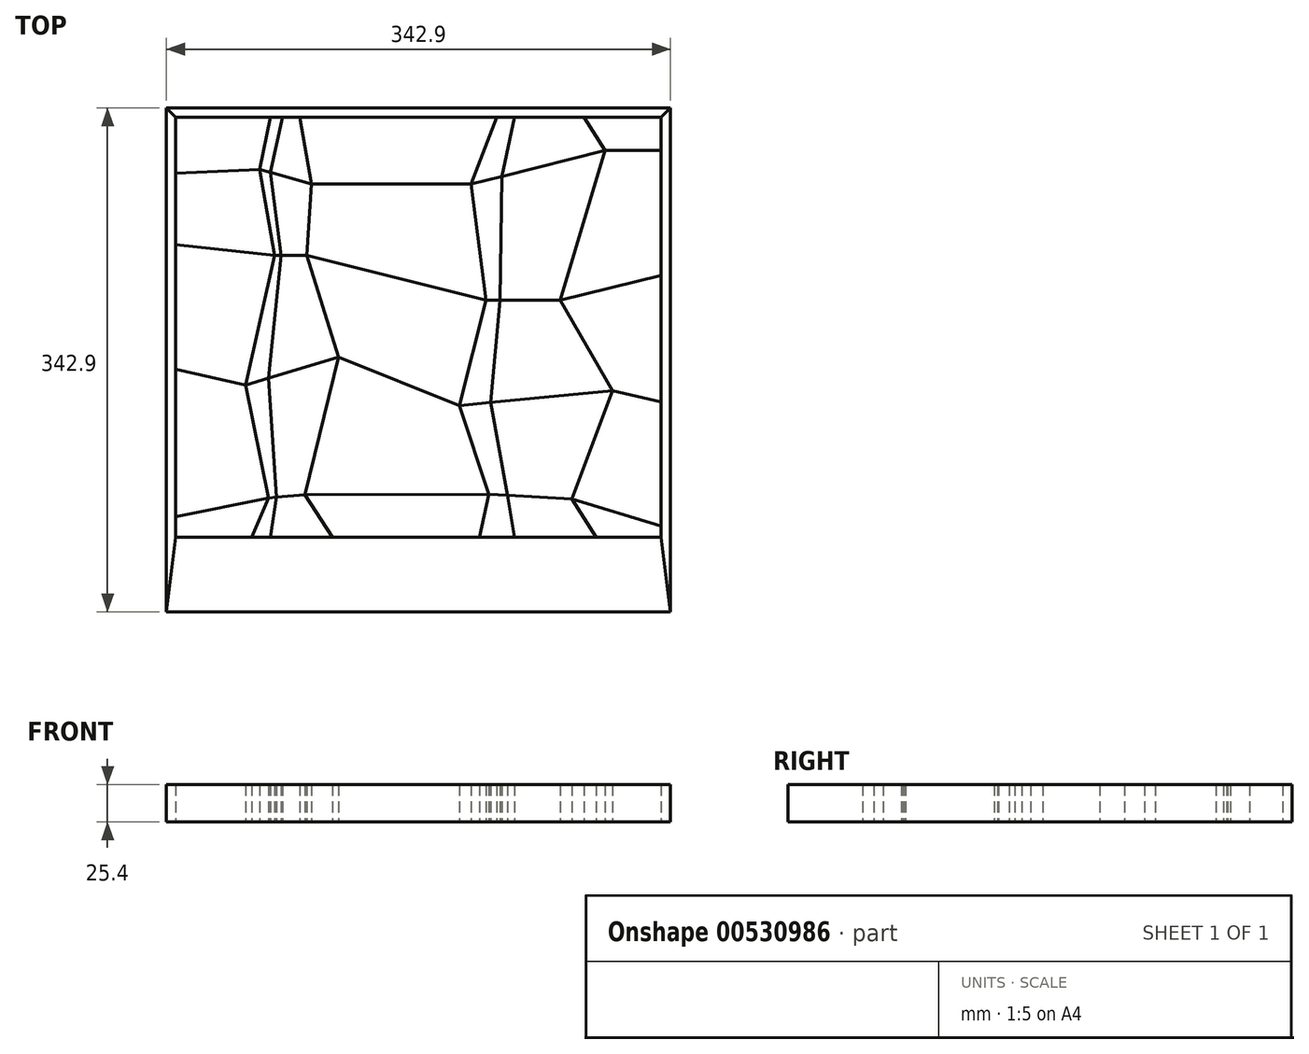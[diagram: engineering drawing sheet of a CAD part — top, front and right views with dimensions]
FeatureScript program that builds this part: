
annotation { "Feature Type Name" : "Feature", "Feature Type Description" : "" }
export const myFeature = defineFeature(function(context is Context, id is Id, definition is map)
    precondition{}
    {
        {
            var Q0;
            Q0=qCreatedBy(makeId("Top.planeOp"),FACE);
            var sketch = newSketch(context, id + "F0", { "sketchPlane" : qUnion([Q0])});
            skLineSegment(sketch, "E0.bottom", {"start": v(171.45, 171.45) * mm, "end": v(-171.45, 171.45) * mm});
            skLineSegment(sketch, "E0.top", {"start": v(171.45, -171.45) * mm, "end": v(-171.45, -171.45) * mm});
            skLineSegment(sketch, "E0.left", {"start": v(171.45, 171.45) * mm, "end": v(171.45, -171.45) * mm});
            skLineSegment(sketch, "E0.right", {"start": v(-171.45, 171.45) * mm, "end": v(-171.45, -171.45) * mm});
            skPoint(sketch, "E0.middle", {"position": v(0, 0) * mm});
            skLineSegment(sketch, "E1.bottom", {"start": v(165.1, 165.1) * mm, "end": v(-165.1, 165.1) * mm});
            skLineSegment(sketch, "E1.top", {"start": v(165.1, -120.65) * mm, "end": v(-165.1, -120.65) * mm});
            skLineSegment(sketch, "E1.left", {"start": v(165.1, 165.1) * mm, "end": v(165.1, -120.65) * mm});
            skLineSegment(sketch, "E1.right", {"start": v(-165.1, 165.1) * mm, "end": v(-165.1, -120.65) * mm});
            skPoint(sketch, "E1.middle", {"position": v(0, 22.23) * mm});
            skLineSegment(sketch, "E2", {"start": v(-165.1, 126.86) * mm, "end": v(-107.99, 129.5) * mm});
            skLineSegment(sketch, "E3", {"start": v(-107.99, 129.5) * mm, "end": v(-97.9, 71.16) * mm});
            skLineSegment(sketch, "E4", {"start": v(-97.9, 71.16) * mm, "end": v(-76, 71.16) * mm});
            skLineSegment(sketch, "E5", {"start": v(-76, 71.16) * mm, "end": v(-72.86, 119.5) * mm});
            skLineSegment(sketch, "E6", {"start": v(-72.86, 119.5) * mm, "end": v(35.82, 119.5) * mm});
            skLineSegment(sketch, "E7", {"start": v(35.82, 119.5) * mm, "end": v(45.94, 40.45) * mm});
            skLineSegment(sketch, "E8", {"start": v(45.94, 40.45) * mm, "end": v(96.28, 40.45) * mm});
            skLineSegment(sketch, "E9", {"start": v(96.28, 40.45) * mm, "end": v(127, 142.54) * mm});
            skLineSegment(sketch, "E10", {"start": v(127, 142.54) * mm, "end": v(165.1, 142.54) * mm});
            skLineSegment(sketch, "E11", {"start": v(-107.99, 129.5) * mm, "end": v(-72.86, 119.5) * mm});
            skLineSegment(sketch, "E12", {"start": v(35.82, 119.5) * mm, "end": v(127, 142.54) * mm});
            skLineSegment(sketch, "E13", {"start": v(-72.86, 119.5) * mm, "end": v(-80.64, 165.1) * mm});
            skLineSegment(sketch, "E14", {"start": v(-107.99, 129.5) * mm, "end": v(-100.88, 165.1) * mm});
            skLineSegment(sketch, "E15", {"start": v(35.82, 119.5) * mm, "end": v(53.18, 165.1) * mm});
            skLineSegment(sketch, "E16", {"start": v(127, 142.54) * mm, "end": v(112.69, 165.1) * mm});
            skLineSegment(sketch, "E17", {"start": v(-165.1, 78.24) * mm, "end": v(-97.9, 71.16) * mm});
            skLineSegment(sketch, "E18", {"start": v(-76, 71.16) * mm, "end": v(45.94, 40.45) * mm});
            skLineSegment(sketch, "E19", {"start": v(96.28, 40.45) * mm, "end": v(165.1, 57.3) * mm});
            skLineSegment(sketch, "E20", {"start": v(45.94, 40.45) * mm, "end": v(27.92, -31.1) * mm});
            skLineSegment(sketch, "E21", {"start": v(96.28, 40.45) * mm, "end": v(132.15, -21.1) * mm});
            skLineSegment(sketch, "E22", {"start": v(-76, 71.16) * mm, "end": v(-54.36, 1.97) * mm});
            skLineSegment(sketch, "E23", {"start": v(-97.9, 71.16) * mm, "end": v(-117.68, -17.1) * mm});
            skLineSegment(sketch, "E24", {"start": v(-117.68, -17.1) * mm, "end": v(-54.36, 1.97) * mm});
            skLineSegment(sketch, "E25", {"start": v(-54.36, 1.97) * mm, "end": v(27.92, -31.1) * mm});
            skLineSegment(sketch, "E26", {"start": v(27.92, -31.1) * mm, "end": v(132.15, -21.1) * mm});
            skLineSegment(sketch, "E27", {"start": v(132.15, -21.1) * mm, "end": v(165.1, -28.47) * mm});
            skLineSegment(sketch, "E28", {"start": v(-117.68, -17.1) * mm, "end": v(-165.1, -6.49) * mm});
            skLineSegment(sketch, "E29", {"start": v(-117.68, -17.1) * mm, "end": v(-102.04, -93.95) * mm});
            skLineSegment(sketch, "E30", {"start": v(-54.36, 1.97) * mm, "end": v(-77.24, -91.93) * mm});
            skLineSegment(sketch, "E31", {"start": v(27.92, -31.1) * mm, "end": v(47.8, -91.37) * mm});
            skLineSegment(sketch, "E32", {"start": v(132.15, -21.1) * mm, "end": v(104.24, -94.5) * mm});
            skLineSegment(sketch, "E33", {"start": v(-165.1, -106.88) * mm, "end": v(-102.04, -93.95) * mm});
            skLineSegment(sketch, "E34", {"start": v(-102.04, -93.95) * mm, "end": v(-77.24, -91.93) * mm});
            skLineSegment(sketch, "E35", {"start": v(-77.24, -91.93) * mm, "end": v(47.8, -91.37) * mm});
            skLineSegment(sketch, "E36", {"start": v(47.8, -91.37) * mm, "end": v(104.24, -94.5) * mm});
            skLineSegment(sketch, "E37", {"start": v(104.24, -94.5) * mm, "end": v(165.1, -113.22) * mm});
            skLineSegment(sketch, "E38", {"start": v(-102.04, -93.95) * mm, "end": v(-113.3, -120.65) * mm});
            skLineSegment(sketch, "E39", {"start": v(-77.24, -91.93) * mm, "end": v(-58.53, -120.65) * mm});
            skLineSegment(sketch, "E40", {"start": v(47.8, -91.37) * mm, "end": v(41.57, -120.65) * mm});
            skLineSegment(sketch, "E41", {"start": v(104.24, -94.5) * mm, "end": v(120.92, -120.65) * mm});
            skLineSegment(sketch, "E42", {"start": v(-171.45, 171.45) * mm, "end": v(-165.1, 165.1) * mm});
            skLineSegment(sketch, "E43", {"start": v(171.45, 171.45) * mm, "end": v(165.1, 165.1) * mm});
            skLineSegment(sketch, "E44", {"start": v(-165.1, -120.65) * mm, "end": v(-171.45, -171.45) * mm});
            skLineSegment(sketch, "E45", {"start": v(165.1, -120.65) * mm, "end": v(171.45, -171.45) * mm});
            skLineSegment(sketch, "E46", {"start": v(-92.53, 165.1) * mm, "end": v(-100.78, 127.45) * mm});
            skLineSegment(sketch, "E47", {"start": v(-100.78, 127.45) * mm, "end": v(-93.48, 71.16) * mm});
            skLineSegment(sketch, "E48", {"start": v(-93.48, 71.16) * mm, "end": v(-101.84, -12.34) * mm});
            skLineSegment(sketch, "E49", {"start": v(-101.84, -12.34) * mm, "end": v(-96.6, -93.5) * mm});
            skLineSegment(sketch, "E50", {"start": v(-96.6, -93.5) * mm, "end": v(-100.88, -120.65) * mm});
            skLineSegment(sketch, "E51", {"start": v(65.3, 165.1) * mm, "end": v(56.81, 124.8) * mm});
            skLineSegment(sketch, "E52", {"start": v(56.81, 124.8) * mm, "end": v(55.33, 40.45) * mm});
            skLineSegment(sketch, "E53", {"start": v(55.33, 40.45) * mm, "end": v(49.27, -29.04) * mm});
            skLineSegment(sketch, "E54", {"start": v(49.27, -29.04) * mm, "end": v(60.5, -92.07) * mm});
            skLineSegment(sketch, "E55", {"start": v(60.5, -92.07) * mm, "end": v(65.22, -120.65) * mm});
            skSolve(sketch);
        }
        {
            var Q0;
            Q0=makeQuery(id+"F0.imprint","IMPRINT",FACE,{"disambiguationData":[TD([[makeQuery(id+"F0.imprint","IMPRINT",EDGE,{"derivedFrom":sQuery(id+"F0.wireOp",EDGE,"E0.bottom")}),1.0]])]});
            var Q1;
            Q1=makeQuery(id+"F0.imprint","IMPRINT",FACE,{"disambiguationData":[TD([[makeQuery(id+"F0.imprint","IMPRINT",EDGE,{"derivedFrom":sQuery(id+"F0.wireOp",EDGE,"E0.top")}),-1.0]])]});
            extrude(context, id + "F1", {"entities" : qUnion([Q0, Q1]), "depth" : 25.4 * mm, "offsetDistance" : 25.4 * mm});
        }
        {
            var Q0;
            Q0=makeQuery(id+"F0.imprint","IMPRINT",FACE,{"disambiguationData":[TD([[makeQuery(id+"F0.imprint","IMPRINT",EDGE,{"derivedFrom":sQuery(id+"F0.wireOp",EDGE,"E0.right")}),1.0]])]});
            var Q1;
            Q1=makeQuery(id+"F0.imprint","IMPRINT",FACE,{"disambiguationData":[TD([[makeQuery(id+"F0.imprint","IMPRINT",EDGE,{"derivedFrom":sQuery(id+"F0.wireOp",EDGE,"E0.left")}),-1.0]])]});
            extrude(context, id + "F2", {"entities" : qUnion([Q0, Q1]), "depth" : 25.4 * mm, "offsetDistance" : 25.4 * mm});
        }
        {
            var Q0;
            {var subQ0=sQuery(id+"F0.wireOp",EDGE,"E13");Q0=makeQuery(id+"F0.imprint","IMPRINT",FACE,{"disambiguationData":[TD([[makeQuery(id+"F0.imprint","IMPRINT",EDGE,{"derivedFrom":subQ0}),1.0]])]});}
            var Q1;
            {var subQ0=sQuery(id+"F0.wireOp",EDGE,"E22");Q1=makeQuery(id+"F0.imprint","IMPRINT",FACE,{"disambiguationData":[TD([[makeQuery(id+"F0.imprint","IMPRINT",EDGE,{"derivedFrom":subQ0}),-1.0]])]});}
            var Q2;
            {var subQ0=sQuery(id+"F0.wireOp",EDGE,"E39");Q2=makeQuery(id+"F0.imprint","IMPRINT",FACE,{"disambiguationData":[TD([[makeQuery(id+"F0.imprint","IMPRINT",EDGE,{"derivedFrom":subQ0}),-1.0]])]});}
            var Q3;
            {var subQ0=sQuery(id+"F0.wireOp",EDGE,"E16");Q3=makeQuery(id+"F0.imprint","IMPRINT",FACE,{"disambiguationData":[TD([[makeQuery(id+"F0.imprint","IMPRINT",EDGE,{"derivedFrom":subQ0}),1.0]])]});}
            var Q4;
            {var subQ0=sQuery(id+"F0.wireOp",EDGE,"E21");Q4=makeQuery(id+"F0.imprint","IMPRINT",FACE,{"disambiguationData":[TD([[makeQuery(id+"F0.imprint","IMPRINT",EDGE,{"derivedFrom":subQ0}),-1.0]])]});}
            var Q5;
            {var subQ0=sQuery(id+"F0.wireOp",EDGE,"E41");Q5=makeQuery(id+"F0.imprint","IMPRINT",FACE,{"disambiguationData":[TD([[makeQuery(id+"F0.imprint","IMPRINT",EDGE,{"derivedFrom":subQ0}),-1.0]])]});}
            extrude(context, id + "F3", {"entities" : qUnion([Q0, Q1, Q2, Q3, Q4, Q5]), "depth" : 25.4 * mm, "offsetDistance" : 25.4 * mm});
        }
        {
            var Q0;
            {var subQ0=sQuery(id+"F0.wireOp",EDGE,"E30");Q0=makeQuery(id+"F0.imprint","IMPRINT",FACE,{"disambiguationData":[TD([[makeQuery(id+"F0.imprint","IMPRINT",EDGE,{"derivedFrom":subQ0}),-1.0]])]});}
            var Q1;
            {var subQ0=sQuery(id+"F0.wireOp",EDGE,"E32");Q1=makeQuery(id+"F0.imprint","IMPRINT",FACE,{"disambiguationData":[TD([[makeQuery(id+"F0.imprint","IMPRINT",EDGE,{"derivedFrom":subQ0}),-1.0]])]});}
            var Q2;
            Q2=makeQuery(id+"F0.imprint","IMPRINT",FACE,{"disambiguationData":[TD([[makeQuery(id+"F0.imprint","IMPRINT",EDGE,{"derivedFrom":sQuery(id+"F0.wireOp",EDGE,"E6")}),1.0]])]});
            var Q3;
            {var subQ4=sQuery(id+"F0.wireOp",EDGE,"E2");Q3=makeQuery(id+"F0.imprint","IMPRINT",FACE,{"disambiguationData":[TD([[makeQuery(id+"F0.imprint","IMPRINT",EDGE,{"derivedFrom":subQ4}),1.0]])]});}
            var Q4;
            Q4=makeQuery(id+"F0.imprint","IMPRINT",FACE,{"disambiguationData":[TD([[makeQuery(id+"F0.imprint","IMPRINT",EDGE,{"derivedFrom":sQuery(id+"F0.wireOp",EDGE,"E18")}),-1.0]])]});
            var Q5;
            {var subQ0=sQuery(id+"F0.wireOp",EDGE,"E19");Q5=makeQuery(id+"F0.imprint","IMPRINT",FACE,{"disambiguationData":[TD([[makeQuery(id+"F0.imprint","IMPRINT",EDGE,{"derivedFrom":subQ0}),-1.0]])]});}
            var Q6;
            {var subQ4=sQuery(id+"F0.wireOp",EDGE,"E10");Q6=makeQuery(id+"F0.imprint","IMPRINT",FACE,{"disambiguationData":[TD([[makeQuery(id+"F0.imprint","IMPRINT",EDGE,{"derivedFrom":subQ4}),1.0]])]});}
            var Q7;
            {var subQ4=sQuery(id+"F0.wireOp",EDGE,"E37");Q7=makeQuery(id+"F0.imprint","IMPRINT",FACE,{"disambiguationData":[TD([[makeQuery(id+"F0.imprint","IMPRINT",EDGE,{"derivedFrom":subQ4}),-1.0]])]});}
            var Q8;
            Q8=makeQuery(id+"F0.imprint","IMPRINT",FACE,{"disambiguationData":[TD([[makeQuery(id+"F0.imprint","IMPRINT",EDGE,{"derivedFrom":sQuery(id+"F0.wireOp",EDGE,"E35")}),-1.0]])]});
            var Q9;
            {var subQ0=sQuery(id+"F0.wireOp",EDGE,"E17");Q9=makeQuery(id+"F0.imprint","IMPRINT",FACE,{"disambiguationData":[TD([[makeQuery(id+"F0.imprint","IMPRINT",EDGE,{"derivedFrom":subQ0}),-1.0]])]});}
            var Q10;
            {var subQ4=sQuery(id+"F0.wireOp",EDGE,"E33");Q10=makeQuery(id+"F0.imprint","IMPRINT",FACE,{"disambiguationData":[TD([[makeQuery(id+"F0.imprint","IMPRINT",EDGE,{"derivedFrom":subQ4}),-1.0]])]});}
            var Q11;
            {var subQ0=sQuery(id+"F0.wireOp",EDGE,"E5");Q11=makeQuery(id+"F0.imprint","IMPRINT",FACE,{"disambiguationData":[TD([[makeQuery(id+"F0.imprint","IMPRINT",EDGE,{"derivedFrom":subQ0}),1.0]])]});}
            var Q12;
            {var subQ0=sQuery(id+"F0.wireOp",EDGE,"E9");Q12=makeQuery(id+"F0.imprint","IMPRINT",FACE,{"disambiguationData":[TD([[makeQuery(id+"F0.imprint","IMPRINT",EDGE,{"derivedFrom":subQ0}),1.0]])]});}
            extrude(context, id + "F4", {"entities" : qUnion([Q0, Q1, Q2, Q3, Q4, Q5, Q6, Q7, Q8, Q9, Q10, Q11, Q12]), "depth" : 25.4 * mm, "offsetDistance" : 25.4 * mm});
        }
        {
            var Q0;
            {var subQ0=sQuery(id+"F0.wireOp",EDGE,"E2");Q0=makeQuery(id+"F0.imprint","IMPRINT",FACE,{"disambiguationData":[TD([[makeQuery(id+"F0.imprint","IMPRINT",EDGE,{"derivedFrom":subQ0}),-1.0]])]});}
            var Q1;
            Q1=makeQuery(id+"F0.imprint","IMPRINT",FACE,{"disambiguationData":[TD([[makeQuery(id+"F0.imprint","IMPRINT",EDGE,{"derivedFrom":sQuery(id+"F0.wireOp",EDGE,"E5")}),-1.0]])]});
            var Q2;
            Q2=makeQuery(id+"F0.imprint","IMPRINT",FACE,{"disambiguationData":[TD([[makeQuery(id+"F0.imprint","IMPRINT",EDGE,{"derivedFrom":sQuery(id+"F0.wireOp",EDGE,"E9")}),-1.0]])]});
            var Q3;
            {var subQ0=sQuery(id+"F0.wireOp",EDGE,"E27");Q3=makeQuery(id+"F0.imprint","IMPRINT",FACE,{"disambiguationData":[TD([[makeQuery(id+"F0.imprint","IMPRINT",EDGE,{"derivedFrom":subQ0}),-1.0]])]});}
            var Q4;
            Q4=makeQuery(id+"F0.imprint","IMPRINT",FACE,{"disambiguationData":[TD([[makeQuery(id+"F0.imprint","IMPRINT",EDGE,{"derivedFrom":sQuery(id+"F0.wireOp",EDGE,"E25")}),-1.0]])]});
            var Q5;
            {var subQ0=sQuery(id+"F0.wireOp",EDGE,"E28");Q5=makeQuery(id+"F0.imprint","IMPRINT",FACE,{"disambiguationData":[TD([[makeQuery(id+"F0.imprint","IMPRINT",EDGE,{"derivedFrom":subQ0}),1.0]])]});}
            extrude(context, id + "F5", {"entities" : qUnion([Q0, Q1, Q2, Q3, Q4, Q5]), "depth" : 25.4 * mm, "offsetDistance" : 25.4 * mm});
        }
        {
            var Q0;
            {var subQ0=sQuery(id+"F0.wireOp",EDGE,"E14");Q0=makeQuery(id+"F0.imprint","IMPRINT",FACE,{"disambiguationData":[TD([[makeQuery(id+"F0.imprint","IMPRINT",EDGE,{"derivedFrom":subQ0}),-1.0]])]});}
            var Q1;
            {var subQ0=sQuery(id+"F0.wireOp",EDGE,"E23");Q1=makeQuery(id+"F0.imprint","IMPRINT",FACE,{"disambiguationData":[TD([[makeQuery(id+"F0.imprint","IMPRINT",EDGE,{"derivedFrom":subQ0}),1.0]])]});}
            var Q2;
            {var subQ0=sQuery(id+"F0.wireOp",EDGE,"E38");Q2=makeQuery(id+"F0.imprint","IMPRINT",FACE,{"disambiguationData":[TD([[makeQuery(id+"F0.imprint","IMPRINT",EDGE,{"derivedFrom":subQ0}),1.0]])]});}
            var Q3;
            {var subQ0=sQuery(id+"F0.wireOp",EDGE,"E15");Q3=makeQuery(id+"F0.imprint","IMPRINT",FACE,{"disambiguationData":[TD([[makeQuery(id+"F0.imprint","IMPRINT",EDGE,{"derivedFrom":subQ0}),-1.0]])]});}
            var Q4;
            {var subQ0=sQuery(id+"F0.wireOp",EDGE,"E20");Q4=makeQuery(id+"F0.imprint","IMPRINT",FACE,{"disambiguationData":[TD([[makeQuery(id+"F0.imprint","IMPRINT",EDGE,{"derivedFrom":subQ0}),1.0]])]});}
            var Q5;
            {var subQ0=sQuery(id+"F0.wireOp",EDGE,"E40");Q5=makeQuery(id+"F0.imprint","IMPRINT",FACE,{"disambiguationData":[TD([[makeQuery(id+"F0.imprint","IMPRINT",EDGE,{"derivedFrom":subQ0}),1.0]])]});}
            extrude(context, id + "F6", {"entities" : qUnion([Q0, Q1, Q2, Q3, Q4, Q5]), "depth" : 25.4 * mm, "offsetDistance" : 25.4 * mm});
        }
        {
            var Q0;
            {var subQ0=sQuery(id+"F0.wireOp",EDGE,"E3");Q0=makeQuery(id+"F0.imprint","IMPRINT",FACE,{"disambiguationData":[TD([[makeQuery(id+"F0.imprint","IMPRINT",EDGE,{"derivedFrom":subQ0}),1.0]])]});}
            var Q1;
            {var subQ0=sQuery(id+"F0.wireOp",EDGE,"E7");Q1=makeQuery(id+"F0.imprint","IMPRINT",FACE,{"disambiguationData":[TD([[makeQuery(id+"F0.imprint","IMPRINT",EDGE,{"derivedFrom":subQ0}),1.0]])]});}
            var Q2;
            {var subQ0=sQuery(id+"F0.wireOp",EDGE,"E31");Q2=makeQuery(id+"F0.imprint","IMPRINT",FACE,{"disambiguationData":[TD([[makeQuery(id+"F0.imprint","IMPRINT",EDGE,{"derivedFrom":subQ0}),1.0]])]});}
            var Q3;
            {var subQ0=sQuery(id+"F0.wireOp",EDGE,"E29");Q3=makeQuery(id+"F0.imprint","IMPRINT",FACE,{"disambiguationData":[TD([[makeQuery(id+"F0.imprint","IMPRINT",EDGE,{"derivedFrom":subQ0}),1.0]])]});}
            extrude(context, id + "F7", {"entities" : qUnion([Q0, Q1, Q2, Q3]), "depth" : 25.4 * mm, "offsetDistance" : 25.4 * mm});
        }
    });
